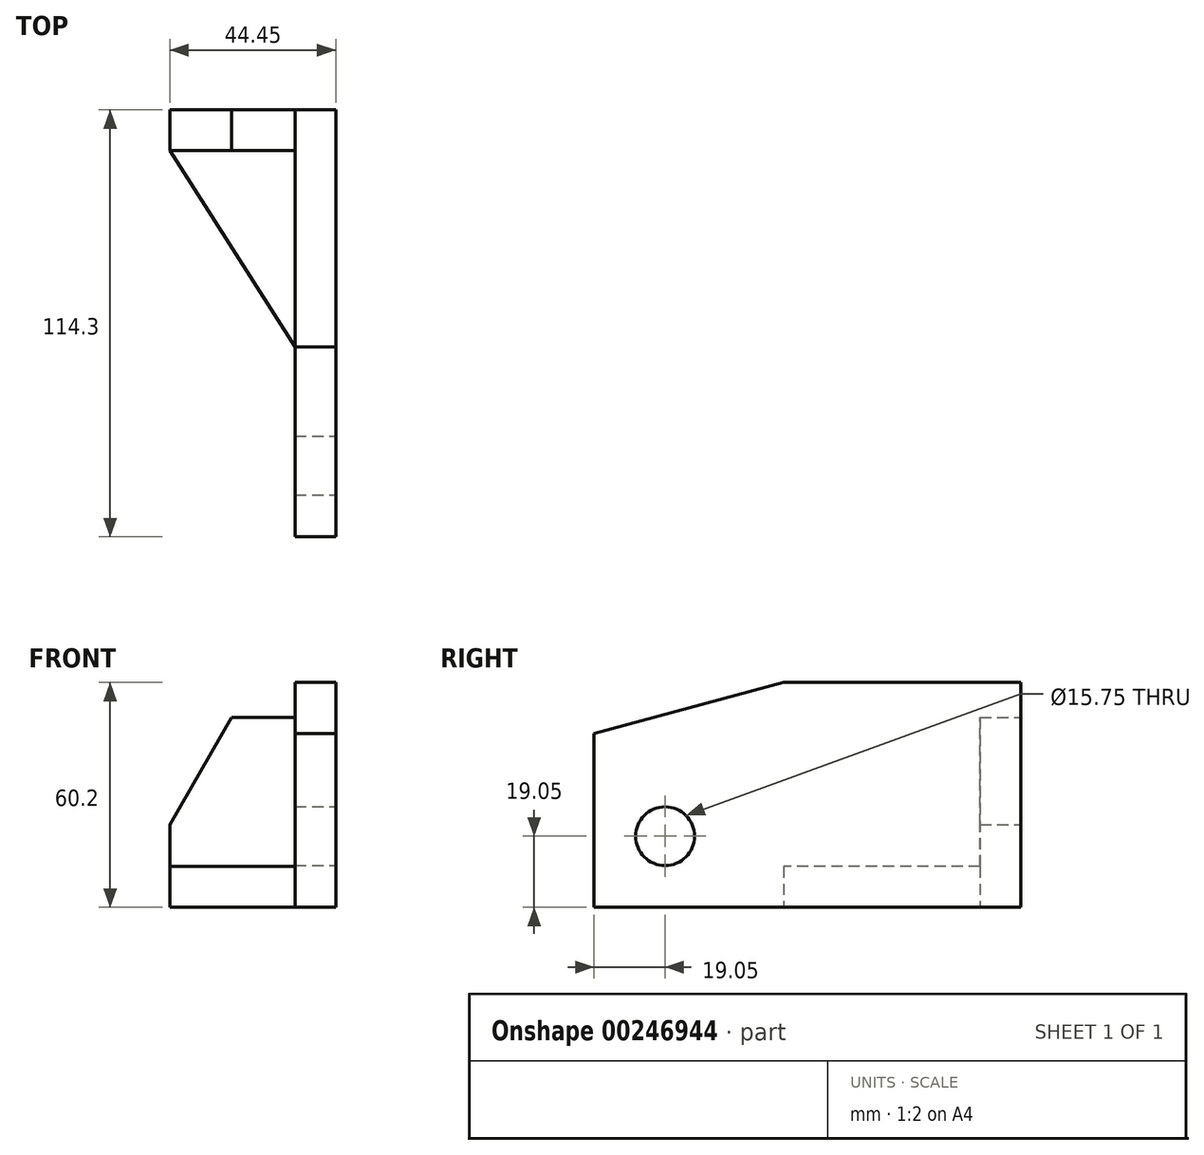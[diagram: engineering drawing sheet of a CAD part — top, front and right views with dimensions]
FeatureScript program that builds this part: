
annotation { "Feature Type Name" : "Feature", "Feature Type Description" : "" }
export const myFeature = defineFeature(function(context is Context, id is Id, definition is map)
    precondition{}
    {
        {
            var Q0;
            Q0=qCreatedBy(makeId("Right.planeOp"),FACE);
            var sketch = newSketch(context, id + "F0", { "sketchPlane" : qUnion([Q0])});
            skLineSegment(sketch, "E0.bottom", {"start": v(0, 0) * mm, "end": v(-114.3, 0) * mm});
            skLineSegment(sketch, "E0.top", {"start": v(0, 60.2) * mm, "end": v(-114.3, 60.2) * mm});
            skLineSegment(sketch, "E0.left", {"start": v(0, 0) * mm, "end": v(0, 60.2) * mm});
            skLineSegment(sketch, "E0.right", {"start": v(-114.3, 0) * mm, "end": v(-114.3, 60.2) * mm});
            skCircle(sketch, "E1", {"center": v(-95.25, 19.05) * mm, "radius": 7.87 * mm});
            skSolve(sketch);
        }
        {
            var Q0;
            Q0=qCreatedBy(makeId("Top.planeOp"),FACE);
            var sketch = newSketch(context, id + "F1", { "sketchPlane" : qUnion([Q0])});
            skLineSegment(sketch, "E2.bottom", {"start": v(0, 0) * mm, "end": v(-44.45, 0) * mm});
            skLineSegment(sketch, "E2.top", {"start": v(0, -63.5) * mm, "end": v(-10.92, -63.5) * mm});
            skLineSegment(sketch, "E2.left", {"start": v(0, 0) * mm, "end": v(0, -63.5) * mm});
            skLineSegment(sketch, "E2.right", {"start": v(-44.45, 0) * mm, "end": v(-44.45, -10.92) * mm});
            skLineSegment(sketch, "E3", {"start": v(-44.45, -10.92) * mm, "end": v(-10.92, -63.5) * mm});
            skSolve(sketch);
        }
        {
            var Q0;
            Q0 = qSketchRegion(id + "F0", true);
            extrude(context, id + "F2", {"entities" : qUnion([Q0]), "oppositeDirection" : true, "depth" : 10.92 * mm});
        }
        {
            var Q0;
            Q0=makeQuery(id+"F2.opExtrude","SWEPT_EDGE",EDGE,{"disambiguationData":[OSD([sQuery(id+"F0.wireOp",EDGE,"E0.top"),sQuery(id+"F0.wireOp",EDGE,"E0.right")])]});
            chamfer(context, id + "F3", {"entities" : qUnion([Q0]), "chamferType" : ChamferType.OFFSET_ANGLE, "width" : 50.8 * mm, "oppositeDirection" : false, "angle" : 15 * degree, "tangentPropagation" : true});
        }
        {
            var Q0;
            Q0 = qSketchRegion(id + "F1", true);
            extrude(context, id + "F4", {"entities" : qUnion([Q0]), "operationType" : NewBodyOperationType.ADD, "depth" : 10.92 * mm});
        }
        {
            var Q0;
            Q0=qCreatedBy(makeId("Front.planeOp"),FACE);
            var sketch = newSketch(context, id + "F5", { "sketchPlane" : qUnion([Q0])});
            skLineSegment(sketch, "E4.bottom", {"start": v(0, 0) * mm, "end": v(-44.45, 0) * mm});
            skLineSegment(sketch, "E4.top", {"start": v(0, 50.8) * mm, "end": v(-44.45, 50.8) * mm});
            skLineSegment(sketch, "E4.left", {"start": v(0, 0) * mm, "end": v(0, 50.8) * mm});
            skLineSegment(sketch, "E4.right", {"start": v(-44.45, 0) * mm, "end": v(-44.45, 50.8) * mm});
            skSolve(sketch);
        }
        {
            var Q0;
            Q0=makeQuery(id+"F5.imprint","IMPRINT",FACE,{"disambiguationData":[TD([[makeQuery(id+"F5.imprint","IMPRINT",EDGE,{"derivedFrom":sQuery(id+"F5.wireOp",EDGE,"E4.bottom")}),-1.0]])]});
            extrude(context, id + "F6", {"entities" : qUnion([Q0]), "operationType" : NewBodyOperationType.ADD, "depth" : 10.92 * mm});
        }
        {
            var Q0;
            Q0=makeQuery(id+"F6.opExtrude","SWEPT_EDGE",EDGE,{"disambiguationData":[OSD([sQuery(id+"F5.wireOp",EDGE,"E4.top"),sQuery(id+"F5.wireOp",EDGE,"E4.right")])]});
            chamfer(context, id + "F7", {"entities" : qUnion([Q0]), "chamferType" : ChamferType.OFFSET_ANGLE, "width" : 28.7 * mm, "oppositeDirection" : false, "angle" : 30 * degree, "tangentPropagation" : true});
        }
    });
